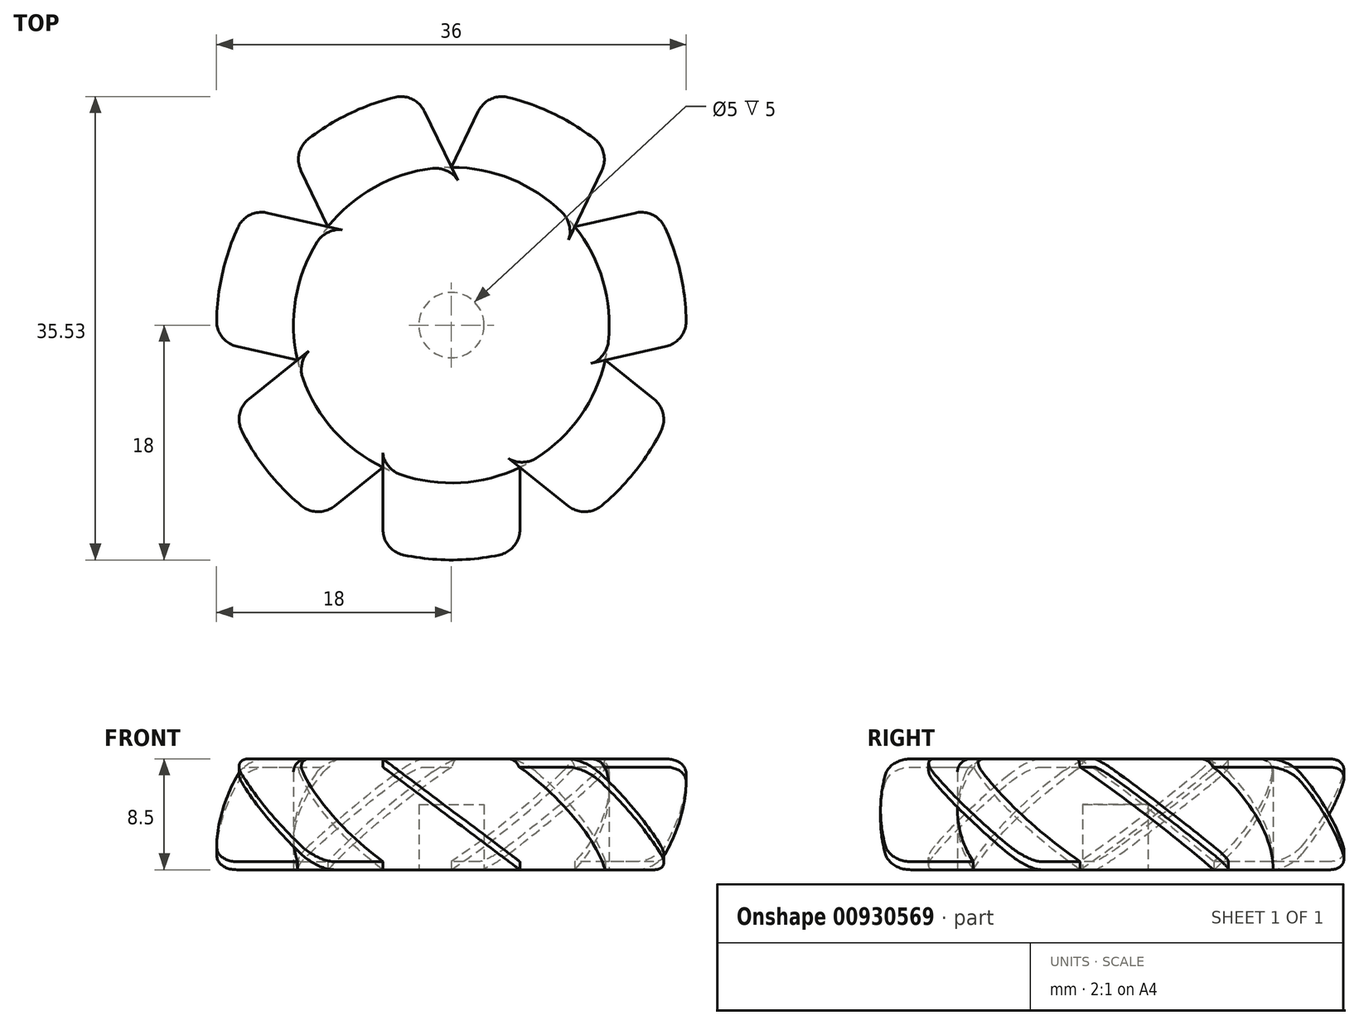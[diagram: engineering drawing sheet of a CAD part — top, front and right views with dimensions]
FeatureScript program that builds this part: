
annotation { "Feature Type Name" : "Feature", "Feature Type Description" : "" }
export const myFeature = defineFeature(function(context is Context, id is Id, definition is map)
    precondition{}
    {
        {
            var Q0;
            Q0=qCreatedBy(makeId("Top.planeOp"),FACE);
            var sketch = newSketch(context, id + "F0", { "sketchPlane" : qUnion([Q0])});
            skCircle(sketch, "E0", {"center": v(0, 0) * mm, "radius": 12.1 * mm, "construction": true});
            skLineSegment(sketch, "E1", {"start": v(0, 12.1) * mm, "end": v(-9.46, 7.54) * mm});
            skLineSegment(sketch, "E2", {"start": v(-9.46, 7.54) * mm, "end": v(-11.8, -2.7) * mm});
            skLineSegment(sketch, "E3", {"start": v(-11.8, -2.7) * mm, "end": v(-5.25, -10.9) * mm});
            skLineSegment(sketch, "E4", {"start": v(-5.25, -10.9) * mm, "end": v(5.25, -10.9) * mm});
            skLineSegment(sketch, "E5", {"start": v(5.25, -10.9) * mm, "end": v(11.8, -2.7) * mm});
            skLineSegment(sketch, "E6", {"start": v(11.8, -2.7) * mm, "end": v(9.46, 7.54) * mm});
            skLineSegment(sketch, "E7", {"start": v(9.46, 7.54) * mm, "end": v(0, 12.1) * mm});
            skSolve(sketch);
        }
        {
            var Q0;
            Q0=qSketchRegion(id+"F0",true);
            extrude(context, id + "F1", {"entities" : qUnion([Q0]), "depth" : 8.5 * mm});
        }
        {
            var Q0;
            Q0=makeQuery(id+"F1.opExtrude","SWEPT_FACE",FACE,{"disambiguationData":[OSD([sQuery(id+"F0.wireOp",EDGE,"E2")])]});
            var sketch = newSketch(context, id + "F2", { "sketchPlane" : qUnion([Q0])});
            skLineSegment(sketch, "E8", {"start": v(-5.25, 8.5) * mm, "end": v(5.25, 0.63) * mm});
            skLineSegment(sketch, "E9", {"start": v(5.25, 0.63) * mm, "end": v(5.25, 0) * mm});
            skLineSegment(sketch, "E10", {"start": v(5.25, 0) * mm, "end": v(-5.25, 7.87) * mm});
            skLineSegment(sketch, "E11", {"start": v(-5.25, 7.87) * mm, "end": v(-5.25, 8.5) * mm});
            skSolve(sketch);
        }
        {
            var Q0;
            Q0=qSketchRegion(id+"F2",true);
            extrude(context, id + "F3", {"entities" : qUnion([Q0]), "operationType" : NewBodyOperationType.ADD, "depth" : 10 * mm});
        }
        {
            var Q0;
            Q0=makeQuery(id+"F1.opExtrude","SWEPT_FACE",FACE,{"disambiguationData":[OSD([sQuery(id+"F0.wireOp",EDGE,"E3")])]});
            var sketch = newSketch(context, id + "F4", { "sketchPlane" : qUnion([Q0])});
            skLineSegment(sketch, "E12", {"start": v(-5.25, 8.5) * mm, "end": v(5.25, 0.63) * mm});
            skLineSegment(sketch, "E13", {"start": v(5.25, 0.63) * mm, "end": v(5.25, 0) * mm});
            skLineSegment(sketch, "E14", {"start": v(5.25, 0) * mm, "end": v(-5.25, 7.87) * mm});
            skLineSegment(sketch, "E15", {"start": v(-5.25, 7.87) * mm, "end": v(-5.25, 8.5) * mm});
            skSolve(sketch);
        }
        {
            var Q0;
            Q0=qSketchRegion(id+"F4",true);
            extrude(context, id + "F5", {"entities" : qUnion([Q0]), "operationType" : NewBodyOperationType.ADD, "depth" : 10 * mm});
        }
        {
            var Q0;
            Q0=makeQuery(id+"F1.opExtrude","SWEPT_FACE",FACE,{"disambiguationData":[OSD([sQuery(id+"F0.wireOp",EDGE,"E4")])]});
            var sketch = newSketch(context, id + "F6", { "sketchPlane" : qUnion([Q0])});
            skLineSegment(sketch, "E16", {"start": v(-5.25, 8.5) * mm, "end": v(5.25, 0.63) * mm});
            skLineSegment(sketch, "E17", {"start": v(5.25, 0.63) * mm, "end": v(5.25, 0) * mm});
            skLineSegment(sketch, "E18", {"start": v(5.25, 0) * mm, "end": v(-5.25, 7.87) * mm});
            skLineSegment(sketch, "E19", {"start": v(-5.25, 7.87) * mm, "end": v(-5.25, 8.5) * mm});
            skSolve(sketch);
        }
        {
            var Q0;
            Q0=qSketchRegion(id+"F6",true);
            extrude(context, id + "F7", {"entities" : qUnion([Q0]), "operationType" : NewBodyOperationType.ADD, "depth" : 10 * mm});
        }
        {
            var Q0;
            Q0=makeQuery(id+"F1.opExtrude","SWEPT_FACE",FACE,{"disambiguationData":[OSD([sQuery(id+"F0.wireOp",EDGE,"E5")])]});
            var sketch = newSketch(context, id + "F8", { "sketchPlane" : qUnion([Q0])});
            skLineSegment(sketch, "E20", {"start": v(-5.25, 8.5) * mm, "end": v(5.25, 0.63) * mm});
            skLineSegment(sketch, "E21", {"start": v(5.25, 0.63) * mm, "end": v(5.25, 0) * mm});
            skLineSegment(sketch, "E22", {"start": v(5.25, 0) * mm, "end": v(-5.25, 7.87) * mm});
            skLineSegment(sketch, "E23", {"start": v(-5.25, 7.87) * mm, "end": v(-5.25, 8.5) * mm});
            skSolve(sketch);
        }
        {
            var Q0;
            Q0=qSketchRegion(id+"F8",true);
            extrude(context, id + "F9", {"entities" : qUnion([Q0]), "operationType" : NewBodyOperationType.ADD, "depth" : 10 * mm});
        }
        {
            var Q0;
            Q0=makeQuery(id+"F1.opExtrude","SWEPT_FACE",FACE,{"disambiguationData":[OSD([sQuery(id+"F0.wireOp",EDGE,"E6")])]});
            var sketch = newSketch(context, id + "F10", { "sketchPlane" : qUnion([Q0])});
            skLineSegment(sketch, "E24", {"start": v(-5.25, 8.5) * mm, "end": v(5.25, 0.63) * mm});
            skLineSegment(sketch, "E25", {"start": v(5.25, 0.63) * mm, "end": v(5.25, 0) * mm});
            skLineSegment(sketch, "E26", {"start": v(5.25, 0) * mm, "end": v(-5.25, 7.87) * mm});
            skLineSegment(sketch, "E27", {"start": v(-5.25, 7.87) * mm, "end": v(-5.25, 8.5) * mm});
            skSolve(sketch);
        }
        {
            var Q0;
            Q0=qSketchRegion(id+"F10",true);
            extrude(context, id + "F11", {"entities" : qUnion([Q0]), "operationType" : NewBodyOperationType.ADD, "depth" : 10 * mm});
        }
        {
            var Q0;
            Q0=makeQuery(id+"F1.opExtrude","SWEPT_FACE",FACE,{"disambiguationData":[OSD([sQuery(id+"F0.wireOp",EDGE,"E7")])]});
            var sketch = newSketch(context, id + "F12", { "sketchPlane" : qUnion([Q0])});
            skLineSegment(sketch, "E28", {"start": v(-5.25, 8.5) * mm, "end": v(5.25, 0.63) * mm});
            skLineSegment(sketch, "E29", {"start": v(5.25, 0.63) * mm, "end": v(5.25, 0) * mm});
            skLineSegment(sketch, "E30", {"start": v(5.25, 0) * mm, "end": v(-5.25, 7.87) * mm});
            skLineSegment(sketch, "E31", {"start": v(-5.25, 7.87) * mm, "end": v(-5.25, 8.5) * mm});
            skSolve(sketch);
        }
        {
            var Q0;
            Q0=qSketchRegion(id+"F12",true);
            extrude(context, id + "F13", {"entities" : qUnion([Q0]), "operationType" : NewBodyOperationType.ADD, "depth" : 10 * mm});
        }
        {
            var Q0;
            Q0=makeQuery(id+"F1.opExtrude","SWEPT_FACE",FACE,{"disambiguationData":[OSD([sQuery(id+"F0.wireOp",EDGE,"E1")])]});
            var sketch = newSketch(context, id + "F14", { "sketchPlane" : qUnion([Q0])});
            skLineSegment(sketch, "E32", {"start": v(-5.25, 8.5) * mm, "end": v(5.25, 0.63) * mm});
            skLineSegment(sketch, "E33", {"start": v(5.25, 0.63) * mm, "end": v(5.25, 0) * mm});
            skLineSegment(sketch, "E34", {"start": v(5.25, 0) * mm, "end": v(-5.25, 7.87) * mm});
            skLineSegment(sketch, "E35", {"start": v(-5.25, 7.87) * mm, "end": v(-5.25, 8.5) * mm});
            skSolve(sketch);
        }
        {
            var Q0;
            Q0=qSketchRegion(id+"F14",true);
            extrude(context, id + "F15", {"entities" : qUnion([Q0]), "operationType" : NewBodyOperationType.ADD, "depth" : 10 * mm});
        }
        {
            var Q0;
            Q0=qCreatedBy(makeId("Top.planeOp"),FACE);
            var sketch = newSketch(context, id + "F16", { "sketchPlane" : qUnion([Q0])});
            skCircle(sketch, "E36", {"center": v(0, 0) * mm, "radius": 12.1 * mm});
            skSolve(sketch);
        }
        {
            var Q0;
            Q0=qSketchRegion(id+"F16",true);
            extrude(context, id + "F17", {"entities" : qUnion([Q0]), "operationType" : NewBodyOperationType.ADD, "depth" : 8.5 * mm});
        }
        {
            var Q0;
            Q0=makeQuery(id+"F17.boolean.opBoolean","MERGE",FACE,{"derivedFrom":[makeQuery(id+"F1.opExtrude","CAP_FACE",FACE,{"disambiguationData":[OSD([sQuery(id+"F0.wireOp",EDGE,"E1"),sQuery(id+"F0.wireOp",EDGE,"E2"),sQuery(id+"F0.wireOp",EDGE,"E3"),sQuery(id+"F0.wireOp",EDGE,"E4"),sQuery(id+"F0.wireOp",EDGE,"E5"),sQuery(id+"F0.wireOp",EDGE,"E6"),sQuery(id+"F0.wireOp",EDGE,"E7")])],"isStart":false}),makeQuery(id+"F17.opExtrude","CAP_FACE",FACE,{"disambiguationData":[OSD([sQuery(id+"F16.wireOp",EDGE,"E36")])],"isStart":false})]});
            var sketch = newSketch(context, id + "F18", { "sketchPlane" : qUnion([Q0])});
            skCircle(sketch, "E37", {"center": v(0, 0) * mm, "radius": 18 * mm});
            skCircle(sketch, "E38", {"center": v(0, 0) * mm, "radius": 25 * mm});
            skSolve(sketch);
        }
        {
            var Q0;
            Q0=qSketchRegion(id+"F18",true);
            var Q1;
            Q1=makeQuery(id+"F17.boolean.opBoolean","MERGE",FACE,{"derivedFrom":[makeQuery(id+"F1.opExtrude","CAP_FACE",FACE,{"disambiguationData":[OSD([sQuery(id+"F0.wireOp",EDGE,"E1"),sQuery(id+"F0.wireOp",EDGE,"E2"),sQuery(id+"F0.wireOp",EDGE,"E3"),sQuery(id+"F0.wireOp",EDGE,"E4"),sQuery(id+"F0.wireOp",EDGE,"E5"),sQuery(id+"F0.wireOp",EDGE,"E6"),sQuery(id+"F0.wireOp",EDGE,"E7")])],"isStart":true}),makeQuery(id+"F17.opExtrude","CAP_FACE",FACE,{"disambiguationData":[OSD([sQuery(id+"F16.wireOp",EDGE,"E36")])],"isStart":true})]});
            extrude(context, id + "F19", {"entities" : qUnion([Q0]), "operationType" : NewBodyOperationType.REMOVE, "endBound" : BoundingType.UP_TO_SURFACE, "oppositeDirection" : true, "endBoundEntityFace" : qUnion([Q1]), "depth" : 25 * mm});
        }
        {
            var Q0;
            Q0=makeQuery(id+"F17.boolean.opBoolean","MERGE",FACE,{"derivedFrom":[makeQuery(id+"F1.opExtrude","CAP_FACE",FACE,{"disambiguationData":[OSD([sQuery(id+"F0.wireOp",EDGE,"E1"),sQuery(id+"F0.wireOp",EDGE,"E2"),sQuery(id+"F0.wireOp",EDGE,"E3"),sQuery(id+"F0.wireOp",EDGE,"E4"),sQuery(id+"F0.wireOp",EDGE,"E5"),sQuery(id+"F0.wireOp",EDGE,"E6"),sQuery(id+"F0.wireOp",EDGE,"E7")])],"isStart":true}),makeQuery(id+"F17.opExtrude","CAP_FACE",FACE,{"disambiguationData":[OSD([sQuery(id+"F16.wireOp",EDGE,"E36")])],"isStart":true})]});
            var sketch = newSketch(context, id + "F20", { "sketchPlane" : qUnion([Q0])});
            skCircle(sketch, "E39", {"center": v(0, 0) * mm, "radius": 2.5 * mm});
            skSolve(sketch);
        }
        {
            var Q0;
            Q0=qSketchRegion(id+"F20",true);
            extrude(context, id + "F21", {"entities" : qUnion([Q0]), "operationType" : NewBodyOperationType.REMOVE, "oppositeDirection" : true, "depth" : 5 * mm});
        }
        {
            var Q0;
            Q0=makeQuery(id+"F19.boolean.opBoolean","INTERSECT",EDGE,{"derivedFrom":[makeQuery(id+"F7.opExtrude","SWEPT_FACE",FACE,{"disambiguationData":[OSD([sQuery(id+"F6.wireOp",EDGE,"E19")])]}),makeQuery(id+"F19.opExtrude","SWEPT_FACE",FACE,{"disambiguationData":[OSD([sQuery(id+"F18.wireOp",EDGE,"E37")])]})]});
            var Q1;
            Q1=makeQuery(id+"F19.boolean.opBoolean","INTERSECT",EDGE,{"derivedFrom":[makeQuery(id+"F7.opExtrude","SWEPT_FACE",FACE,{"disambiguationData":[OSD([sQuery(id+"F6.wireOp",EDGE,"E17")])]}),makeQuery(id+"F19.opExtrude","SWEPT_FACE",FACE,{"disambiguationData":[OSD([sQuery(id+"F18.wireOp",EDGE,"E37")])]})]});
            var Q2;
            Q2=makeQuery(id+"F19.boolean.opBoolean","INTERSECT",EDGE,{"derivedFrom":[makeQuery(id+"F9.opExtrude","SWEPT_FACE",FACE,{"disambiguationData":[OSD([sQuery(id+"F8.wireOp",EDGE,"E23")])]}),makeQuery(id+"F19.opExtrude","SWEPT_FACE",FACE,{"disambiguationData":[OSD([sQuery(id+"F18.wireOp",EDGE,"E37")])]})]});
            var Q3;
            Q3=makeQuery(id+"F19.boolean.opBoolean","INTERSECT",EDGE,{"derivedFrom":[makeQuery(id+"F9.opExtrude","SWEPT_FACE",FACE,{"disambiguationData":[OSD([sQuery(id+"F8.wireOp",EDGE,"E21")])]}),makeQuery(id+"F19.opExtrude","SWEPT_FACE",FACE,{"disambiguationData":[OSD([sQuery(id+"F18.wireOp",EDGE,"E37")])]})]});
            var Q4;
            Q4=makeQuery(id+"F19.boolean.opBoolean","INTERSECT",EDGE,{"derivedFrom":[makeQuery(id+"F11.opExtrude","SWEPT_FACE",FACE,{"disambiguationData":[OSD([sQuery(id+"F10.wireOp",EDGE,"E27")])]}),makeQuery(id+"F19.opExtrude","SWEPT_FACE",FACE,{"disambiguationData":[OSD([sQuery(id+"F18.wireOp",EDGE,"E37")])]})]});
            var Q5;
            Q5=makeQuery(id+"F19.boolean.opBoolean","INTERSECT",EDGE,{"derivedFrom":[makeQuery(id+"F11.opExtrude","SWEPT_FACE",FACE,{"disambiguationData":[OSD([sQuery(id+"F10.wireOp",EDGE,"E25")])]}),makeQuery(id+"F19.opExtrude","SWEPT_FACE",FACE,{"disambiguationData":[OSD([sQuery(id+"F18.wireOp",EDGE,"E37")])]})]});
            var Q6;
            Q6=makeQuery(id+"F19.boolean.opBoolean","INTERSECT",EDGE,{"derivedFrom":[makeQuery(id+"F13.opExtrude","SWEPT_FACE",FACE,{"disambiguationData":[OSD([sQuery(id+"F12.wireOp",EDGE,"E31")])]}),makeQuery(id+"F19.opExtrude","SWEPT_FACE",FACE,{"disambiguationData":[OSD([sQuery(id+"F18.wireOp",EDGE,"E37")])]})]});
            var Q7;
            Q7=makeQuery(id+"F19.boolean.opBoolean","INTERSECT",EDGE,{"derivedFrom":[makeQuery(id+"F13.opExtrude","SWEPT_FACE",FACE,{"disambiguationData":[OSD([sQuery(id+"F12.wireOp",EDGE,"E29")])]}),makeQuery(id+"F19.opExtrude","SWEPT_FACE",FACE,{"disambiguationData":[OSD([sQuery(id+"F18.wireOp",EDGE,"E37")])]})]});
            var Q8;
            Q8=makeQuery(id+"F19.boolean.opBoolean","INTERSECT",EDGE,{"derivedFrom":[makeQuery(id+"F15.opExtrude","SWEPT_FACE",FACE,{"disambiguationData":[OSD([sQuery(id+"F14.wireOp",EDGE,"E35")])]}),makeQuery(id+"F19.opExtrude","SWEPT_FACE",FACE,{"disambiguationData":[OSD([sQuery(id+"F18.wireOp",EDGE,"E37")])]})]});
            var Q9;
            Q9=makeQuery(id+"F19.boolean.opBoolean","INTERSECT",EDGE,{"derivedFrom":[makeQuery(id+"F15.opExtrude","SWEPT_FACE",FACE,{"disambiguationData":[OSD([sQuery(id+"F14.wireOp",EDGE,"E33")])]}),makeQuery(id+"F19.opExtrude","SWEPT_FACE",FACE,{"disambiguationData":[OSD([sQuery(id+"F18.wireOp",EDGE,"E37")])]})]});
            var Q10;
            Q10=makeQuery(id+"F19.boolean.opBoolean","INTERSECT",EDGE,{"derivedFrom":[makeQuery(id+"F3.opExtrude","SWEPT_FACE",FACE,{"disambiguationData":[OSD([sQuery(id+"F2.wireOp",EDGE,"E11")])]}),makeQuery(id+"F19.opExtrude","SWEPT_FACE",FACE,{"disambiguationData":[OSD([sQuery(id+"F18.wireOp",EDGE,"E37")])]})]});
            var Q11;
            Q11=makeQuery(id+"F19.boolean.opBoolean","INTERSECT",EDGE,{"derivedFrom":[makeQuery(id+"F3.opExtrude","SWEPT_FACE",FACE,{"disambiguationData":[OSD([sQuery(id+"F2.wireOp",EDGE,"E9")])]}),makeQuery(id+"F19.opExtrude","SWEPT_FACE",FACE,{"disambiguationData":[OSD([sQuery(id+"F18.wireOp",EDGE,"E37")])]})]});
            var Q12;
            Q12=makeQuery(id+"F19.boolean.opBoolean","INTERSECT",EDGE,{"derivedFrom":[makeQuery(id+"F5.opExtrude","SWEPT_FACE",FACE,{"disambiguationData":[OSD([sQuery(id+"F4.wireOp",EDGE,"E15")])]}),makeQuery(id+"F19.opExtrude","SWEPT_FACE",FACE,{"disambiguationData":[OSD([sQuery(id+"F18.wireOp",EDGE,"E37")])]})]});
            var Q13;
            Q13=makeQuery(id+"F19.boolean.opBoolean","INTERSECT",EDGE,{"derivedFrom":[makeQuery(id+"F5.opExtrude","SWEPT_FACE",FACE,{"disambiguationData":[OSD([sQuery(id+"F4.wireOp",EDGE,"E13")])]}),makeQuery(id+"F19.opExtrude","SWEPT_FACE",FACE,{"disambiguationData":[OSD([sQuery(id+"F18.wireOp",EDGE,"E37")])]})]});
            fillet(context, id + "F22", {"entities" : qUnion([Q0, Q1, Q2, Q3, Q4, Q5, Q6, Q7, Q8, Q9, Q10, Q11, Q12, Q13]), "radius" : 2 * mm, "tangentPropagation" : true, "allowEdgeOverflow" : false});
        }
        {
            var Q0;
            {var subQ0=sQuery(id+"F16.wireOp",EDGE,"E36");Q0=makeQuery(id+"F17.boolean.opBoolean","SPLIT",EDGE,{"disambiguationData":[TD([makeQuery(id+"F1.opExtrude","CAP_FACE",FACE,{"disambiguationData":[OSD([sQuery(id+"F0.wireOp",EDGE,"E1"),sQuery(id+"F0.wireOp",EDGE,"E2"),sQuery(id+"F0.wireOp",EDGE,"E3"),sQuery(id+"F0.wireOp",EDGE,"E4"),sQuery(id+"F0.wireOp",EDGE,"E5"),sQuery(id+"F0.wireOp",EDGE,"E6"),sQuery(id+"F0.wireOp",EDGE,"E7")])],"isStart":false}),makeQuery(id+"F9.opExtrude","SWEPT_FACE",FACE,{"disambiguationData":[OSD([sQuery(id+"F8.wireOp",EDGE,"E20")])]}),makeQuery(id+"F9.opExtrude","SWEPT_FACE",FACE,{"disambiguationData":[OSD([sQuery(id+"F8.wireOp",EDGE,"E23")])]}),makeQuery(id+"F11.opExtrude","SWEPT_FACE",FACE,{"disambiguationData":[OSD([sQuery(id+"F10.wireOp",EDGE,"E24")])]}),makeQuery(id+"F11.opExtrude","SWEPT_FACE",FACE,{"disambiguationData":[OSD([sQuery(id+"F10.wireOp",EDGE,"E27")])]}),makeQuery(id+"F17.opExtrude","SWEPT_FACE",FACE,{"disambiguationData":[OSD([subQ0])]}),makeQuery(id+"F17.opExtrude","CAP_FACE",FACE,{"disambiguationData":[OSD([subQ0])],"isStart":false})])],"derivedFrom":makeQuery(id+"F17.opExtrude","CAP_EDGE",EDGE,{"disambiguationData":[OSD([subQ0])],"isStart":false})});}
            var Q1;
            {var subQ0=sQuery(id+"F16.wireOp",EDGE,"E36");Q1=makeQuery(id+"F17.boolean.opBoolean","SPLIT",EDGE,{"disambiguationData":[TD([makeQuery(id+"F1.opExtrude","CAP_FACE",FACE,{"disambiguationData":[OSD([sQuery(id+"F0.wireOp",EDGE,"E1"),sQuery(id+"F0.wireOp",EDGE,"E2"),sQuery(id+"F0.wireOp",EDGE,"E3"),sQuery(id+"F0.wireOp",EDGE,"E4"),sQuery(id+"F0.wireOp",EDGE,"E5"),sQuery(id+"F0.wireOp",EDGE,"E6"),sQuery(id+"F0.wireOp",EDGE,"E7")])],"isStart":false}),makeQuery(id+"F11.opExtrude","SWEPT_FACE",FACE,{"disambiguationData":[OSD([sQuery(id+"F10.wireOp",EDGE,"E24")])]}),makeQuery(id+"F11.opExtrude","SWEPT_FACE",FACE,{"disambiguationData":[OSD([sQuery(id+"F10.wireOp",EDGE,"E27")])]}),makeQuery(id+"F13.opExtrude","SWEPT_FACE",FACE,{"disambiguationData":[OSD([sQuery(id+"F12.wireOp",EDGE,"E28")])]}),makeQuery(id+"F13.opExtrude","SWEPT_FACE",FACE,{"disambiguationData":[OSD([sQuery(id+"F12.wireOp",EDGE,"E31")])]}),makeQuery(id+"F17.opExtrude","SWEPT_FACE",FACE,{"disambiguationData":[OSD([subQ0])]}),makeQuery(id+"F17.opExtrude","CAP_FACE",FACE,{"disambiguationData":[OSD([subQ0])],"isStart":false})])],"derivedFrom":makeQuery(id+"F17.opExtrude","CAP_EDGE",EDGE,{"disambiguationData":[OSD([subQ0])],"isStart":false})});}
            var Q2;
            {var subQ0=sQuery(id+"F16.wireOp",EDGE,"E36");Q2=makeQuery(id+"F17.boolean.opBoolean","SPLIT",EDGE,{"disambiguationData":[TD([makeQuery(id+"F1.opExtrude","CAP_FACE",FACE,{"disambiguationData":[OSD([sQuery(id+"F0.wireOp",EDGE,"E1"),sQuery(id+"F0.wireOp",EDGE,"E2"),sQuery(id+"F0.wireOp",EDGE,"E3"),sQuery(id+"F0.wireOp",EDGE,"E4"),sQuery(id+"F0.wireOp",EDGE,"E5"),sQuery(id+"F0.wireOp",EDGE,"E6"),sQuery(id+"F0.wireOp",EDGE,"E7")])],"isStart":false}),makeQuery(id+"F13.opExtrude","SWEPT_FACE",FACE,{"disambiguationData":[OSD([sQuery(id+"F12.wireOp",EDGE,"E28")])]}),makeQuery(id+"F13.opExtrude","SWEPT_FACE",FACE,{"disambiguationData":[OSD([sQuery(id+"F12.wireOp",EDGE,"E31")])]}),makeQuery(id+"F15.opExtrude","SWEPT_FACE",FACE,{"disambiguationData":[OSD([sQuery(id+"F14.wireOp",EDGE,"E32")])]}),makeQuery(id+"F15.opExtrude","SWEPT_FACE",FACE,{"disambiguationData":[OSD([sQuery(id+"F14.wireOp",EDGE,"E35")])]}),makeQuery(id+"F17.opExtrude","SWEPT_FACE",FACE,{"disambiguationData":[OSD([subQ0])]}),makeQuery(id+"F17.opExtrude","CAP_FACE",FACE,{"disambiguationData":[OSD([subQ0])],"isStart":false})])],"derivedFrom":makeQuery(id+"F17.opExtrude","CAP_EDGE",EDGE,{"disambiguationData":[OSD([subQ0])],"isStart":false})});}
            var Q3;
            {var subQ0=sQuery(id+"F16.wireOp",EDGE,"E36");Q3=makeQuery(id+"F17.boolean.opBoolean","SPLIT",EDGE,{"disambiguationData":[TD([makeQuery(id+"F1.opExtrude","CAP_FACE",FACE,{"disambiguationData":[OSD([sQuery(id+"F0.wireOp",EDGE,"E1"),sQuery(id+"F0.wireOp",EDGE,"E2"),sQuery(id+"F0.wireOp",EDGE,"E3"),sQuery(id+"F0.wireOp",EDGE,"E4"),sQuery(id+"F0.wireOp",EDGE,"E5"),sQuery(id+"F0.wireOp",EDGE,"E6"),sQuery(id+"F0.wireOp",EDGE,"E7")])],"isStart":false}),makeQuery(id+"F3.opExtrude","SWEPT_FACE",FACE,{"disambiguationData":[OSD([sQuery(id+"F2.wireOp",EDGE,"E8")])]}),makeQuery(id+"F3.opExtrude","SWEPT_FACE",FACE,{"disambiguationData":[OSD([sQuery(id+"F2.wireOp",EDGE,"E11")])]}),makeQuery(id+"F15.opExtrude","SWEPT_FACE",FACE,{"disambiguationData":[OSD([sQuery(id+"F14.wireOp",EDGE,"E32")])]}),makeQuery(id+"F15.opExtrude","SWEPT_FACE",FACE,{"disambiguationData":[OSD([sQuery(id+"F14.wireOp",EDGE,"E35")])]}),makeQuery(id+"F17.opExtrude","SWEPT_FACE",FACE,{"disambiguationData":[OSD([subQ0])]}),makeQuery(id+"F17.opExtrude","CAP_FACE",FACE,{"disambiguationData":[OSD([subQ0])],"isStart":false})])],"derivedFrom":makeQuery(id+"F17.opExtrude","CAP_EDGE",EDGE,{"disambiguationData":[OSD([subQ0])],"isStart":false})});}
            var Q4;
            {var subQ0=sQuery(id+"F16.wireOp",EDGE,"E36");Q4=makeQuery(id+"F17.boolean.opBoolean","SPLIT",EDGE,{"disambiguationData":[TD([makeQuery(id+"F1.opExtrude","CAP_FACE",FACE,{"disambiguationData":[OSD([sQuery(id+"F0.wireOp",EDGE,"E1"),sQuery(id+"F0.wireOp",EDGE,"E2"),sQuery(id+"F0.wireOp",EDGE,"E3"),sQuery(id+"F0.wireOp",EDGE,"E4"),sQuery(id+"F0.wireOp",EDGE,"E5"),sQuery(id+"F0.wireOp",EDGE,"E6"),sQuery(id+"F0.wireOp",EDGE,"E7")])],"isStart":false}),makeQuery(id+"F3.opExtrude","SWEPT_FACE",FACE,{"disambiguationData":[OSD([sQuery(id+"F2.wireOp",EDGE,"E8")])]}),makeQuery(id+"F3.opExtrude","SWEPT_FACE",FACE,{"disambiguationData":[OSD([sQuery(id+"F2.wireOp",EDGE,"E11")])]}),makeQuery(id+"F5.opExtrude","SWEPT_FACE",FACE,{"disambiguationData":[OSD([sQuery(id+"F4.wireOp",EDGE,"E12")])]}),makeQuery(id+"F5.opExtrude","SWEPT_FACE",FACE,{"disambiguationData":[OSD([sQuery(id+"F4.wireOp",EDGE,"E15")])]}),makeQuery(id+"F17.opExtrude","SWEPT_FACE",FACE,{"disambiguationData":[OSD([subQ0])]}),makeQuery(id+"F17.opExtrude","CAP_FACE",FACE,{"disambiguationData":[OSD([subQ0])],"isStart":false})])],"derivedFrom":makeQuery(id+"F17.opExtrude","CAP_EDGE",EDGE,{"disambiguationData":[OSD([subQ0])],"isStart":false})});}
            var Q5;
            {var subQ0=sQuery(id+"F16.wireOp",EDGE,"E36");Q5=makeQuery(id+"F17.boolean.opBoolean","SPLIT",EDGE,{"disambiguationData":[TD([makeQuery(id+"F1.opExtrude","CAP_FACE",FACE,{"disambiguationData":[OSD([sQuery(id+"F0.wireOp",EDGE,"E1"),sQuery(id+"F0.wireOp",EDGE,"E2"),sQuery(id+"F0.wireOp",EDGE,"E3"),sQuery(id+"F0.wireOp",EDGE,"E4"),sQuery(id+"F0.wireOp",EDGE,"E5"),sQuery(id+"F0.wireOp",EDGE,"E6"),sQuery(id+"F0.wireOp",EDGE,"E7")])],"isStart":false}),makeQuery(id+"F5.opExtrude","SWEPT_FACE",FACE,{"disambiguationData":[OSD([sQuery(id+"F4.wireOp",EDGE,"E12")])]}),makeQuery(id+"F5.opExtrude","SWEPT_FACE",FACE,{"disambiguationData":[OSD([sQuery(id+"F4.wireOp",EDGE,"E15")])]}),makeQuery(id+"F7.opExtrude","SWEPT_FACE",FACE,{"disambiguationData":[OSD([sQuery(id+"F6.wireOp",EDGE,"E16")])]}),makeQuery(id+"F7.opExtrude","SWEPT_FACE",FACE,{"disambiguationData":[OSD([sQuery(id+"F6.wireOp",EDGE,"E19")])]}),makeQuery(id+"F17.opExtrude","SWEPT_FACE",FACE,{"disambiguationData":[OSD([subQ0])]}),makeQuery(id+"F17.opExtrude","CAP_FACE",FACE,{"disambiguationData":[OSD([subQ0])],"isStart":false})])],"derivedFrom":makeQuery(id+"F17.opExtrude","CAP_EDGE",EDGE,{"disambiguationData":[OSD([subQ0])],"isStart":false})});}
            var Q6;
            {var subQ0=sQuery(id+"F16.wireOp",EDGE,"E36");Q6=makeQuery(id+"F17.boolean.opBoolean","SPLIT",EDGE,{"disambiguationData":[TD([makeQuery(id+"F1.opExtrude","CAP_FACE",FACE,{"disambiguationData":[OSD([sQuery(id+"F0.wireOp",EDGE,"E1"),sQuery(id+"F0.wireOp",EDGE,"E2"),sQuery(id+"F0.wireOp",EDGE,"E3"),sQuery(id+"F0.wireOp",EDGE,"E4"),sQuery(id+"F0.wireOp",EDGE,"E5"),sQuery(id+"F0.wireOp",EDGE,"E6"),sQuery(id+"F0.wireOp",EDGE,"E7")])],"isStart":false}),makeQuery(id+"F7.opExtrude","SWEPT_FACE",FACE,{"disambiguationData":[OSD([sQuery(id+"F6.wireOp",EDGE,"E16")])]}),makeQuery(id+"F7.opExtrude","SWEPT_FACE",FACE,{"disambiguationData":[OSD([sQuery(id+"F6.wireOp",EDGE,"E19")])]}),makeQuery(id+"F9.opExtrude","SWEPT_FACE",FACE,{"disambiguationData":[OSD([sQuery(id+"F8.wireOp",EDGE,"E20")])]}),makeQuery(id+"F9.opExtrude","SWEPT_FACE",FACE,{"disambiguationData":[OSD([sQuery(id+"F8.wireOp",EDGE,"E23")])]}),makeQuery(id+"F17.opExtrude","SWEPT_FACE",FACE,{"disambiguationData":[OSD([subQ0])]}),makeQuery(id+"F17.opExtrude","CAP_FACE",FACE,{"disambiguationData":[OSD([subQ0])],"isStart":false})])],"derivedFrom":makeQuery(id+"F17.opExtrude","CAP_EDGE",EDGE,{"disambiguationData":[OSD([subQ0])],"isStart":false})});}
            fillet(context, id + "F23", {"entities" : qUnion([Q0, Q1, Q2, Q3, Q4, Q5, Q6]), "radius" : 1 * mm, "tangentPropagation" : true, "allowEdgeOverflow" : false});
        }
    });
